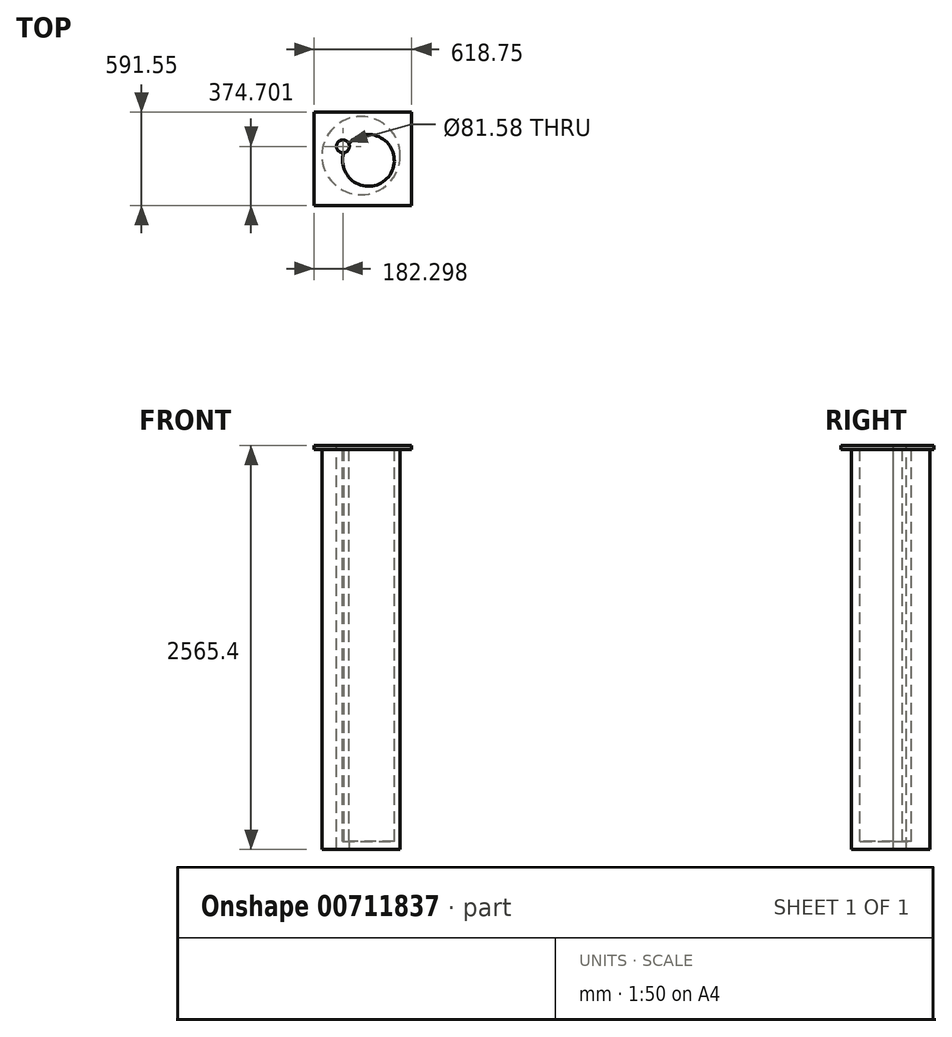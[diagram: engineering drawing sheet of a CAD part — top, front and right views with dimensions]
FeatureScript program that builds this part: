
annotation { "Feature Type Name" : "Feature", "Feature Type Description" : "" }
export const myFeature = defineFeature(function(context is Context, id is Id, definition is map)
    precondition{}
    {
        {
            var Q0;
            Q0=qCreatedBy(makeId("Top.planeOp"),FACE);
            var sketch = newSketch(context, id + "F0", { "sketchPlane" : qUnion([Q0])});
            skCircle(sketch, "E0", {"center": v(0, 0) * mm, "radius": 159.46 * mm});
            skCircle(sketch, "E1", {"center": v(0, 0) * mm, "radius": 3.97 * mm});
            skLineSegment(sketch, "E2.bottom", {"start": v(0, 0) * mm, "end": v(73.32, 0) * mm});
            skLineSegment(sketch, "E2.top", {"start": v(0, 74.7) * mm, "end": v(73.32, 74.7) * mm});
            skLineSegment(sketch, "E2.left", {"start": v(0, 0) * mm, "end": v(0, 74.7) * mm});
            skLineSegment(sketch, "E2.right", {"start": v(73.32, 0) * mm, "end": v(73.32, 74.7) * mm});
            skLineSegment(sketch, "E3.bottom", {"start": v(0, 74.7) * mm, "end": v(-70.96, 74.7) * mm});
            skLineSegment(sketch, "E3.top", {"start": v(0, -70.64) * mm, "end": v(-70.96, -70.64) * mm});
            skLineSegment(sketch, "E3.left", {"start": v(0, 74.7) * mm, "end": v(0, -70.64) * mm});
            skLineSegment(sketch, "E3.right", {"start": v(-70.96, 74.7) * mm, "end": v(-70.96, -70.64) * mm});
            skLineSegment(sketch, "E4.bottom", {"start": v(0, -70.64) * mm, "end": v(-59.77, -70.64) * mm});
            skLineSegment(sketch, "E4.top", {"start": v(0, -78.11) * mm, "end": v(-59.77, -78.11) * mm});
            skLineSegment(sketch, "E4.left", {"start": v(0, -70.64) * mm, "end": v(0, -78.11) * mm});
            skLineSegment(sketch, "E4.right", {"start": v(-59.77, -70.64) * mm, "end": v(-59.77, -78.11) * mm});
            skLineSegment(sketch, "E5.bottom", {"start": v(73.32, 0) * mm, "end": v(0, 0) * mm});
            skLineSegment(sketch, "E5.top", {"start": v(73.32, -78.11) * mm, "end": v(0, -78.11) * mm});
            skLineSegment(sketch, "E5.left", {"start": v(73.32, 0) * mm, "end": v(73.32, -78.11) * mm});
            skLineSegment(sketch, "E5.right", {"start": v(0, 0) * mm, "end": v(0, -78.11) * mm});
            skPoint(sketch, "E6.oppositeSnap0", {"position": v(-70.96, 2.02) * mm});
            skLineSegment(sketch, "E6.bottom", {"start": v(0, 0) * mm, "end": v(-70.96, 0) * mm});
            skLineSegment(sketch, "E6.top", {"start": v(0, 0) * mm, "end": v(-70.96, 0) * mm});
            skLineSegment(sketch, "E6.left", {"start": v(0, 0) * mm, "end": v(0, 0) * mm});
            skLineSegment(sketch, "E6.right", {"start": v(-70.96, 0) * mm, "end": v(-70.96, 0) * mm});
            skLineSegment(sketch, "E7.bottom", {"start": v(92.37, 97.37) * mm, "end": v(-59.77, 97.37) * mm});
            skLineSegment(sketch, "E7.top", {"start": v(92.37, -78.11) * mm, "end": v(-59.77, -78.11) * mm});
            skLineSegment(sketch, "E7.left", {"start": v(92.37, 97.37) * mm, "end": v(92.37, -78.11) * mm});
            skLineSegment(sketch, "E7.right", {"start": v(-59.77, 97.37) * mm, "end": v(-59.77, -78.11) * mm});
            skLineSegment(sketch, "E8.bottom", {"start": v(-59.77, 97.37) * mm, "end": v(-70.96, 97.37) * mm});
            skLineSegment(sketch, "E8.top", {"start": v(-59.77, -70.64) * mm, "end": v(-70.96, -70.64) * mm});
            skLineSegment(sketch, "E8.left", {"start": v(-59.77, 97.37) * mm, "end": v(-59.77, -70.64) * mm});
            skLineSegment(sketch, "E8.right", {"start": v(-70.96, 97.37) * mm, "end": v(-70.96, -70.64) * mm});
            skLineSegment(sketch, "E9.bottom", {"start": v(92.37, 97.37) * mm, "end": v(-47.68, 97.37) * mm});
            skLineSegment(sketch, "E9.top", {"start": v(92.37, -92.25) * mm, "end": v(-47.68, -92.25) * mm});
            skLineSegment(sketch, "E9.left", {"start": v(92.37, 97.37) * mm, "end": v(92.37, -92.25) * mm});
            skLineSegment(sketch, "E9.right", {"start": v(-47.68, 97.37) * mm, "end": v(-47.68, -92.25) * mm});
            skLineSegment(sketch, "E10.bottom", {"start": v(-23.79, -115.3) * mm, "end": v(-59.77, -115.3) * mm});
            skLineSegment(sketch, "E10.top", {"start": v(-23.79, -78.11) * mm, "end": v(-59.77, -78.11) * mm});
            skLineSegment(sketch, "E10.left", {"start": v(-23.79, -115.3) * mm, "end": v(-23.79, -78.11) * mm});
            skLineSegment(sketch, "E10.right", {"start": v(-59.77, -115.3) * mm, "end": v(-59.77, -78.11) * mm});
            skSolve(sketch);
        }
        {
            var Q0;
            Q0=makeQuery(id+"F0.imprint","IMPRINT",FACE,{"disambiguationData":[TD([[makeQuery(id+"F0.imprint","IMPRINT",EDGE,{"derivedFrom":sQuery(id+"F0.wireOp",EDGE,"E0")}),1.0]])]});
            var sketch = newSketch(context, id + "F1", { "sketchPlane" : qUnion([Q0])});
            skLineSegment(sketch, "E11.bottom", {"start": v(-21.25, 53.53) * mm, "end": v(0, 53.53) * mm});
            skLineSegment(sketch, "E11.top", {"start": v(-21.25, -69.67) * mm, "end": v(0, -69.67) * mm});
            skLineSegment(sketch, "E11.left", {"start": v(-21.25, 53.53) * mm, "end": v(-21.25, -69.67) * mm});
            skLineSegment(sketch, "E11.right", {"start": v(0, 53.53) * mm, "end": v(0, -69.67) * mm});
            skLineSegment(sketch, "E12.bottom", {"start": v(0, -69.67) * mm, "end": v(74.53, -69.67) * mm});
            skLineSegment(sketch, "E12.top", {"start": v(0, 76.63) * mm, "end": v(74.53, 76.63) * mm});
            skLineSegment(sketch, "E12.left", {"start": v(0, -69.67) * mm, "end": v(0, 76.63) * mm});
            skLineSegment(sketch, "E12.right", {"start": v(74.53, -69.67) * mm, "end": v(74.53, 76.63) * mm});
            skLineSegment(sketch, "E13.bottom", {"start": v(74.53, -69.67) * mm, "end": v(74.53, -69.67) * mm});
            skLineSegment(sketch, "E13.top", {"start": v(74.53, -80.15) * mm, "end": v(74.53, -80.15) * mm});
            skLineSegment(sketch, "E13.left", {"start": v(74.53, -69.67) * mm, "end": v(74.53, -80.15) * mm});
            skLineSegment(sketch, "E13.right", {"start": v(74.53, -69.67) * mm, "end": v(74.53, -80.15) * mm});
            skPoint(sketch, "E14.oppositeSnap0", {"position": v(-10.62, -69.67) * mm});
            skLineSegment(sketch, "E14.bottom", {"start": v(74.53, -80.15) * mm, "end": v(-80.32, -80.15) * mm});
            skLineSegment(sketch, "E14.top", {"start": v(74.53, -69.67) * mm, "end": v(-80.32, -69.67) * mm});
            skLineSegment(sketch, "E14.left", {"start": v(74.53, -80.15) * mm, "end": v(74.53, -69.67) * mm});
            skLineSegment(sketch, "E14.right", {"start": v(-80.32, -80.15) * mm, "end": v(-80.32, -69.67) * mm});
            skLineSegment(sketch, "E15.bottom", {"start": v(-80.32, -69.67) * mm, "end": v(0, -69.67) * mm});
            skLineSegment(sketch, "E15.top", {"start": v(-80.32, 76.63) * mm, "end": v(0, 76.63) * mm});
            skLineSegment(sketch, "E15.left", {"start": v(-80.32, -69.67) * mm, "end": v(-80.32, 76.63) * mm});
            skSolve(sketch);
        }
        {
            var Q0;
            Q0 = qSketchRegion(id + "F1", true);
            extrude(context, id + "F2", {"entities" : qUnion([Q0]), "depth" : 25.4 * mm, "offsetDistance" : 25.4 * mm});
        }
        {
            var Q0;
            Q0=qCreatedBy(makeId("Top.planeOp"),FACE);
            var sketch = newSketch(context, id + "F3", { "sketchPlane" : qUnion([Q0])});
            skCircle(sketch, "E16", {"center": v(-47.12, 30.55) * mm, "radius": 248.02 * mm});
            skSolve(sketch);
        }
        {
            var Q0;
            Q0 = qSketchRegion(id + "F3", true);
            extrude(context, id + "F4", {"entities" : qUnion([Q0]), "operationType" : NewBodyOperationType.ADD, "depth" : -2540 * mm, "offsetDistance" : 25.4 * mm});
        }
        {
            var Q0;
            {var subQ0=sQuery(id+"F3.wireOp",EDGE,"E16");Q0=makeQuery(id+"F4.boolean.opBoolean","SPLIT",FACE,{"disambiguationData":[TD([makeQuery(id+"F2.opExtrude","SWEPT_FACE",FACE,{"disambiguationData":[OSD([sQuery(id+"F1.wireOp",EDGE,"E14.bottom")])]})])],"derivedFrom":makeQuery(id+"F4.opExtrude","CAP_FACE",FACE,{"disambiguationData":[OSD([subQ0])],"isStart":true})});}
            var sketch = newSketch(context, id + "F5", { "sketchPlane" : qUnion([Q0])});
            skLineSegment(sketch, "E17.bottom", {"start": v(-23.82, 125.05) * mm, "end": v(274.46, 125.05) * mm});
            skLineSegment(sketch, "E17.top", {"start": v(-23.82, 306.2) * mm, "end": v(274.46, 306.2) * mm});
            skLineSegment(sketch, "E17.left", {"start": v(-23.82, 125.05) * mm, "end": v(-23.82, 306.2) * mm});
            skLineSegment(sketch, "E17.right", {"start": v(274.46, 125.05) * mm, "end": v(274.46, 306.2) * mm});
            skLineSegment(sketch, "E18.bottom", {"start": v(274.46, 125.05) * mm, "end": v(-344.29, 125.05) * mm});
            skLineSegment(sketch, "E18.top", {"start": v(274.46, -285.35) * mm, "end": v(-344.29, -285.35) * mm});
            skLineSegment(sketch, "E18.left", {"start": v(274.46, 125.05) * mm, "end": v(274.46, -285.35) * mm});
            skLineSegment(sketch, "E18.right", {"start": v(-344.29, 125.05) * mm, "end": v(-344.29, -285.35) * mm});
            skLineSegment(sketch, "E19.bottom", {"start": v(-344.29, 125.05) * mm, "end": v(-23.82, 125.05) * mm});
            skLineSegment(sketch, "E19.top", {"start": v(-344.29, 306.2) * mm, "end": v(-23.82, 306.2) * mm});
            skLineSegment(sketch, "E19.left", {"start": v(-344.29, 125.05) * mm, "end": v(-344.29, 306.2) * mm});
            skLineSegment(sketch, "E20.top", {"start": v(-23.82, -285.35) * mm, "end": v(274.46, -285.35) * mm});
            skLineSegment(sketch, "E20.left", {"start": v(-23.82, 125.05) * mm, "end": v(-23.82, -285.35) * mm});
            skLineSegment(sketch, "E21.bottom", {"start": v(-23.82, -80.15) * mm, "end": v(-344.29, -80.15) * mm});
            skLineSegment(sketch, "E21.top", {"start": v(-23.82, -80.15) * mm, "end": v(-344.29, -80.15) * mm});
            skLineSegment(sketch, "E21.left", {"start": v(-23.82, -80.15) * mm, "end": v(-23.82, -80.15) * mm});
            skLineSegment(sketch, "E21.right", {"start": v(-344.29, -80.15) * mm, "end": v(-344.29, -80.15) * mm});
            skLineSegment(sketch, "E22.bottom", {"start": v(-23.82, -80.15) * mm, "end": v(274.46, -80.15) * mm});
            skLineSegment(sketch, "E22.top", {"start": v(-23.82, -80.15) * mm, "end": v(274.46, -80.15) * mm});
            skLineSegment(sketch, "E22.right", {"start": v(274.46, -80.15) * mm, "end": v(274.46, -80.15) * mm});
            skLineSegment(sketch, "E23.bottom", {"start": v(95.98, -80.15) * mm, "end": v(102.35, -80.15) * mm});
            skLineSegment(sketch, "E23.top", {"start": v(95.98, 306.2) * mm, "end": v(102.35, 306.2) * mm});
            skLineSegment(sketch, "E23.left", {"start": v(95.98, -80.15) * mm, "end": v(95.98, 306.2) * mm});
            skLineSegment(sketch, "E23.right", {"start": v(102.35, -80.15) * mm, "end": v(102.35, 306.2) * mm});
            skLineSegment(sketch, "E24.bottom", {"start": v(102.35, -80.15) * mm, "end": v(102.35, -80.15) * mm});
            skLineSegment(sketch, "E24.top", {"start": v(102.35, -285.35) * mm, "end": v(102.35, -285.35) * mm});
            skLineSegment(sketch, "E24.left", {"start": v(102.35, -80.15) * mm, "end": v(102.35, -285.35) * mm});
            skLineSegment(sketch, "E24.right", {"start": v(102.35, -80.15) * mm, "end": v(102.35, -285.35) * mm});
            skSolve(sketch);
        }
        {
            var Q0;
            Q0 = qSketchRegion(id + "F5", true);
            extrude(context, id + "F6", {"entities" : qUnion([Q0]), "operationType" : NewBodyOperationType.ADD, "depth" : 25.4 * mm, "offsetDistance" : 25.4 * mm});
        }
        {
            var Q0;
            Q0=makeQuery(id+"F6.boolean.opBoolean","MERGE",FACE,{"derivedFrom":[makeQuery(id+"F2.opExtrude","CAP_FACE",FACE,{"disambiguationData":[OSD([sQuery(id+"F1.wireOp",EDGE,"E11.bottom"),sQuery(id+"F1.wireOp",EDGE,"E11.left"),sQuery(id+"F1.wireOp",EDGE,"E12.top"),sQuery(id+"F1.wireOp",EDGE,"E12.right"),sQuery(id+"F1.wireOp",EDGE,"E14.bottom"),sQuery(id+"F1.wireOp",EDGE,"E14.left"),sQuery(id+"F1.wireOp",EDGE,"E14.right"),sQuery(id+"F1.wireOp",EDGE,"E15.bottom"),sQuery(id+"F1.wireOp",EDGE,"E15.top"),sQuery(id+"F1.wireOp",EDGE,"E15.left"),sQuery(id+"F1.wireOp",EDGE,"E12.left")])],"isStart":false}),makeQuery(id+"F6.opExtrude","CAP_FACE",FACE,{"disambiguationData":[OSD([sQuery(id+"F5.wireOp",EDGE,"E17.top"),sQuery(id+"F5.wireOp",EDGE,"E17.right"),sQuery(id+"F5.wireOp",EDGE,"E18.top"),sQuery(id+"F5.wireOp",EDGE,"E18.right"),sQuery(id+"F5.wireOp",EDGE,"E19.top"),sQuery(id+"F5.wireOp",EDGE,"E19.left"),sQuery(id+"F5.wireOp",EDGE,"E17.bottom"),sQuery(id+"F5.wireOp",EDGE,"E20.top"),sQuery(id+"F5.wireOp",EDGE,"E20.left"),sQuery(id+"F5.wireOp",EDGE,"E18.left"),sQuery(id+"F5.wireOp",EDGE,"E22.top"),sQuery(id+"F5.wireOp",EDGE,"E23.bottom"),sQuery(id+"F5.wireOp",EDGE,"E23.top"),sQuery(id+"F5.wireOp",EDGE,"E23.right")])],"isStart":false})]});
            var sketch = newSketch(context, id + "F7", { "sketchPlane" : qUnion([Q0])});
            skCircle(sketch, "E25", {"center": v(-162, 89.35) * mm, "radius": 40.79 * mm});
            skSolve(sketch);
        }
        {
            var Q0;
            Q0 = qSketchRegion(id + "F7", true);
            extrude(context, id + "F8", {"entities" : qUnion([Q0]), "operationType" : NewBodyOperationType.REMOVE, "endBound" : BoundingType.THROUGH_ALL, "oppositeDirection" : true, "depth" : 25.4 * mm, "offsetDistance" : 25.4 * mm});
        }
        {
            var Q0;
            Q0=makeQuery(id+"F6.boolean.opBoolean","MERGE",FACE,{"derivedFrom":[makeQuery(id+"F2.opExtrude","CAP_FACE",FACE,{"disambiguationData":[OSD([sQuery(id+"F1.wireOp",EDGE,"E11.bottom"),sQuery(id+"F1.wireOp",EDGE,"E11.left"),sQuery(id+"F1.wireOp",EDGE,"E12.top"),sQuery(id+"F1.wireOp",EDGE,"E12.right"),sQuery(id+"F1.wireOp",EDGE,"E14.bottom"),sQuery(id+"F1.wireOp",EDGE,"E14.left"),sQuery(id+"F1.wireOp",EDGE,"E14.right"),sQuery(id+"F1.wireOp",EDGE,"E15.bottom"),sQuery(id+"F1.wireOp",EDGE,"E15.top"),sQuery(id+"F1.wireOp",EDGE,"E15.left"),sQuery(id+"F1.wireOp",EDGE,"E12.left")])],"isStart":false}),makeQuery(id+"F6.opExtrude","CAP_FACE",FACE,{"disambiguationData":[OSD([sQuery(id+"F5.wireOp",EDGE,"E17.top"),sQuery(id+"F5.wireOp",EDGE,"E17.right"),sQuery(id+"F5.wireOp",EDGE,"E18.top"),sQuery(id+"F5.wireOp",EDGE,"E18.right"),sQuery(id+"F5.wireOp",EDGE,"E19.top"),sQuery(id+"F5.wireOp",EDGE,"E19.left"),sQuery(id+"F5.wireOp",EDGE,"E17.bottom"),sQuery(id+"F5.wireOp",EDGE,"E20.top"),sQuery(id+"F5.wireOp",EDGE,"E20.left"),sQuery(id+"F5.wireOp",EDGE,"E18.left"),sQuery(id+"F5.wireOp",EDGE,"E22.top"),sQuery(id+"F5.wireOp",EDGE,"E23.bottom"),sQuery(id+"F5.wireOp",EDGE,"E23.top"),sQuery(id+"F5.wireOp",EDGE,"E23.right")])],"isStart":false})]});
            var sketch = newSketch(context, id + "F9", { "sketchPlane" : qUnion([Q0])});
            skCircle(sketch, "E26", {"center": v(0, 0) * mm, "radius": 164.16 * mm});
            skSolve(sketch);
        }
        {
            var Q0;
            Q0 = qSketchRegion(id + "F9", true);
            extrude(context, id + "F10", {"entities" : qUnion([Q0]), "operationType" : NewBodyOperationType.REMOVE, "oppositeDirection" : true, "depth" : 2514.6 * mm, "offsetDistance" : 25.4 * mm});
        }
    });
